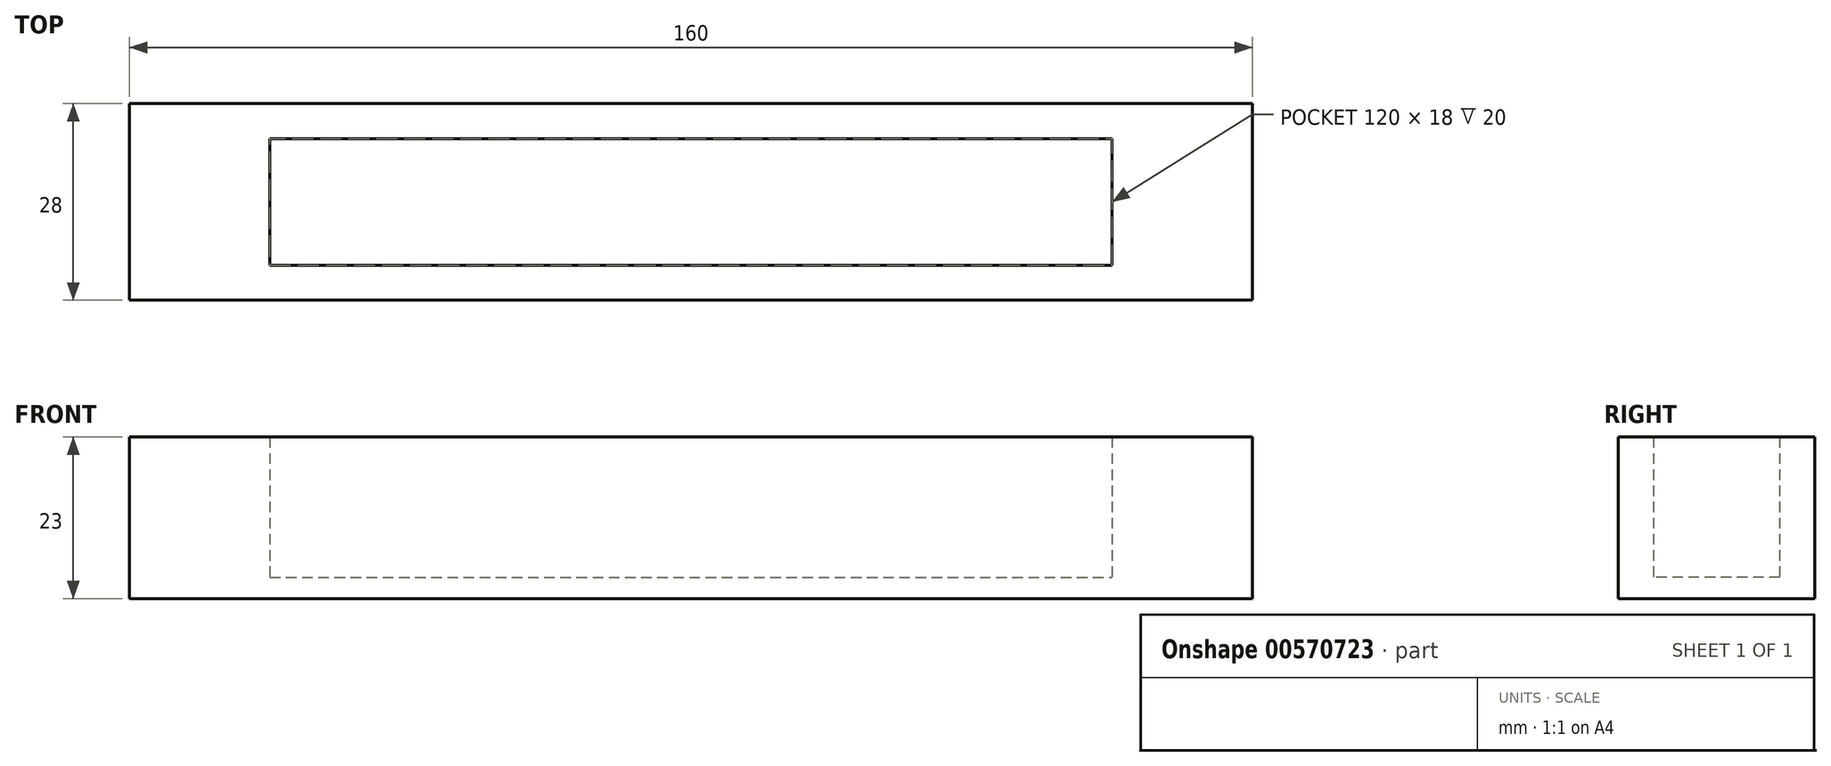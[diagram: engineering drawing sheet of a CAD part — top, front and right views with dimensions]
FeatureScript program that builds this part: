
annotation { "Feature Type Name" : "Feature", "Feature Type Description" : "" }
export const myFeature = defineFeature(function(context is Context, id is Id, definition is map)
    precondition{}
    {
        {
            var Q0;
            Q0=qCreatedBy(makeId("Top.planeOp"),FACE);
            var sketch = newSketch(context, id + "F0", { "sketchPlane" : qUnion([Q0])});
            skLineSegment(sketch, "E0.bottom", {"start": v(80, -14) * mm, "end": v(-80, -14) * mm});
            skLineSegment(sketch, "E0.top", {"start": v(80, 14) * mm, "end": v(-80, 14) * mm});
            skLineSegment(sketch, "E0.left", {"start": v(80, -14) * mm, "end": v(80, 14) * mm});
            skLineSegment(sketch, "E0.right", {"start": v(-80, -14) * mm, "end": v(-80, 14) * mm});
            skPoint(sketch, "E0.middle", {"position": v(0, 0) * mm});
            skLineSegment(sketch, "E1.bottom", {"start": v(60, -9) * mm, "end": v(-60, -9) * mm});
            skLineSegment(sketch, "E1.top", {"start": v(60, 9) * mm, "end": v(-60, 9) * mm});
            skLineSegment(sketch, "E1.left", {"start": v(60, -9) * mm, "end": v(60, 9) * mm});
            skLineSegment(sketch, "E1.right", {"start": v(-60, -9) * mm, "end": v(-60, 9) * mm});
            skLineSegment(sketch, "E2.bottom", {"start": v(100, -40) * mm, "end": v(-100, -40) * mm});
            skLineSegment(sketch, "E2.top", {"start": v(100, 40) * mm, "end": v(-100, 40) * mm});
            skLineSegment(sketch, "E2.left", {"start": v(100, -40) * mm, "end": v(100, 40) * mm});
            skLineSegment(sketch, "E2.right", {"start": v(-100, -40) * mm, "end": v(-100, 40) * mm});
            skLineSegment(sketch, "E3.bottom", {"start": v(49, -14.05) * mm, "end": v(-49, -14.05) * mm});
            skLineSegment(sketch, "E3.top", {"start": v(49, 14.05) * mm, "end": v(-49, 14.05) * mm});
            skLineSegment(sketch, "E3.left", {"start": v(49, -14.05) * mm, "end": v(49, 14.05) * mm});
            skLineSegment(sketch, "E3.right", {"start": v(-49, -14.05) * mm, "end": v(-49, 14.05) * mm});
            skSolve(sketch);
        }
        {
            var Q0;
            {var subQ4=sQuery(id+"F0.wireOp",EDGE,"E0.right");Q0=makeQuery(id+"F0.imprint","IMPRINT",FACE,{"disambiguationData":[TD([[makeQuery(id+"F0.imprint","IMPRINT",EDGE,{"derivedFrom":subQ4}),-1.0]])]});}
            var Q1;
            {var subQ0=sQuery(id+"F0.wireOp",EDGE,"E3.left");var subQ1=sQuery(id+"F0.wireOp",EDGE,"E0.top");var subQ2=makeQuery(id+"F0.imprint","INTERSECT",VERTEX,{"derivedFrom":[subQ1,subQ0]});Q1=makeQuery(id+"F0.imprint","IMPRINT",FACE,{"disambiguationData":[TD([[makeQuery(id+"F0.imprint","IMPRINT",EDGE,{"disambiguationData":[TD([[subQ2,-1.0]])],"derivedFrom":subQ1}),1.0]])]});}
            var Q2;
            {var subQ0=sQuery(id+"F0.wireOp",EDGE,"E3.left");var subQ1=sQuery(id+"F0.wireOp",EDGE,"E1.bottom");var subQ2=makeQuery(id+"F0.imprint","INTERSECT",VERTEX,{"derivedFrom":[subQ1,subQ0]});Q2=makeQuery(id+"F0.imprint","IMPRINT",FACE,{"disambiguationData":[TD([[makeQuery(id+"F0.imprint","IMPRINT",EDGE,{"disambiguationData":[TD([[subQ2,-1.0]])],"derivedFrom":subQ1}),-1.0]])]});}
            var Q3;
            {var subQ0=sQuery(id+"F0.wireOp",EDGE,"E1.right");Q3=makeQuery(id+"F0.imprint","IMPRINT",FACE,{"disambiguationData":[TD([[makeQuery(id+"F0.imprint","IMPRINT",EDGE,{"derivedFrom":subQ0}),-1.0]])]});}
            var Q4;
            {var subQ0=sQuery(id+"F0.wireOp",EDGE,"E3.left");var subQ1=sQuery(id+"F0.wireOp",EDGE,"E0.bottom");var subQ2=makeQuery(id+"F0.imprint","INTERSECT",VERTEX,{"derivedFrom":[subQ1,subQ0]});Q4=makeQuery(id+"F0.imprint","IMPRINT",FACE,{"disambiguationData":[TD([[makeQuery(id+"F0.imprint","IMPRINT",EDGE,{"disambiguationData":[TD([[subQ2,-1.0]])],"derivedFrom":subQ1}),-1.0]])]});}
            var Q5;
            {var subQ0=sQuery(id+"F0.wireOp",EDGE,"E0.left");Q5=makeQuery(id+"F0.imprint","IMPRINT",FACE,{"disambiguationData":[TD([[makeQuery(id+"F0.imprint","IMPRINT",EDGE,{"derivedFrom":subQ0}),1.0]])]});}
            var Q6;
            {var subQ0=sQuery(id+"F0.wireOp",EDGE,"E1.left");Q6=makeQuery(id+"F0.imprint","IMPRINT",FACE,{"disambiguationData":[TD([[makeQuery(id+"F0.imprint","IMPRINT",EDGE,{"derivedFrom":subQ0}),1.0]])]});}
            extrude(context, id + "F1", {"entities" : qUnion([Q0, Q1, Q2, Q3, Q4, Q5, Q6]), "depth" : 3 * mm, "offsetDistance" : 25 * mm});
        }
        {
            var Q0;
            {var subQ4=sQuery(id+"F0.wireOp",EDGE,"E0.right");Q0=makeQuery(id+"F0.imprint","IMPRINT",FACE,{"disambiguationData":[TD([[makeQuery(id+"F0.imprint","IMPRINT",EDGE,{"derivedFrom":subQ4}),-1.0]])]});}
            var Q1;
            {var subQ0=sQuery(id+"F0.wireOp",EDGE,"E3.left");var subQ1=sQuery(id+"F0.wireOp",EDGE,"E0.top");var subQ2=makeQuery(id+"F0.imprint","INTERSECT",VERTEX,{"derivedFrom":[subQ1,subQ0]});Q1=makeQuery(id+"F0.imprint","IMPRINT",FACE,{"disambiguationData":[TD([[makeQuery(id+"F0.imprint","IMPRINT",EDGE,{"disambiguationData":[TD([[subQ2,-1.0]])],"derivedFrom":subQ1}),1.0]])]});}
            var Q2;
            {var subQ0=sQuery(id+"F0.wireOp",EDGE,"E3.left");var subQ1=sQuery(id+"F0.wireOp",EDGE,"E0.bottom");var subQ2=makeQuery(id+"F0.imprint","INTERSECT",VERTEX,{"derivedFrom":[subQ1,subQ0]});Q2=makeQuery(id+"F0.imprint","IMPRINT",FACE,{"disambiguationData":[TD([[makeQuery(id+"F0.imprint","IMPRINT",EDGE,{"disambiguationData":[TD([[subQ2,-1.0]])],"derivedFrom":subQ1}),-1.0]])]});}
            var Q3;
            {var subQ0=sQuery(id+"F0.wireOp",EDGE,"E0.left");Q3=makeQuery(id+"F0.imprint","IMPRINT",FACE,{"disambiguationData":[TD([[makeQuery(id+"F0.imprint","IMPRINT",EDGE,{"derivedFrom":subQ0}),1.0]])]});}
            extrude(context, id + "F2", {"entities" : qUnion([Q0, Q1, Q2, Q3]), "operationType" : NewBodyOperationType.ADD, "depth" : 23 * mm, "offsetDistance" : 25 * mm});
        }
    });
